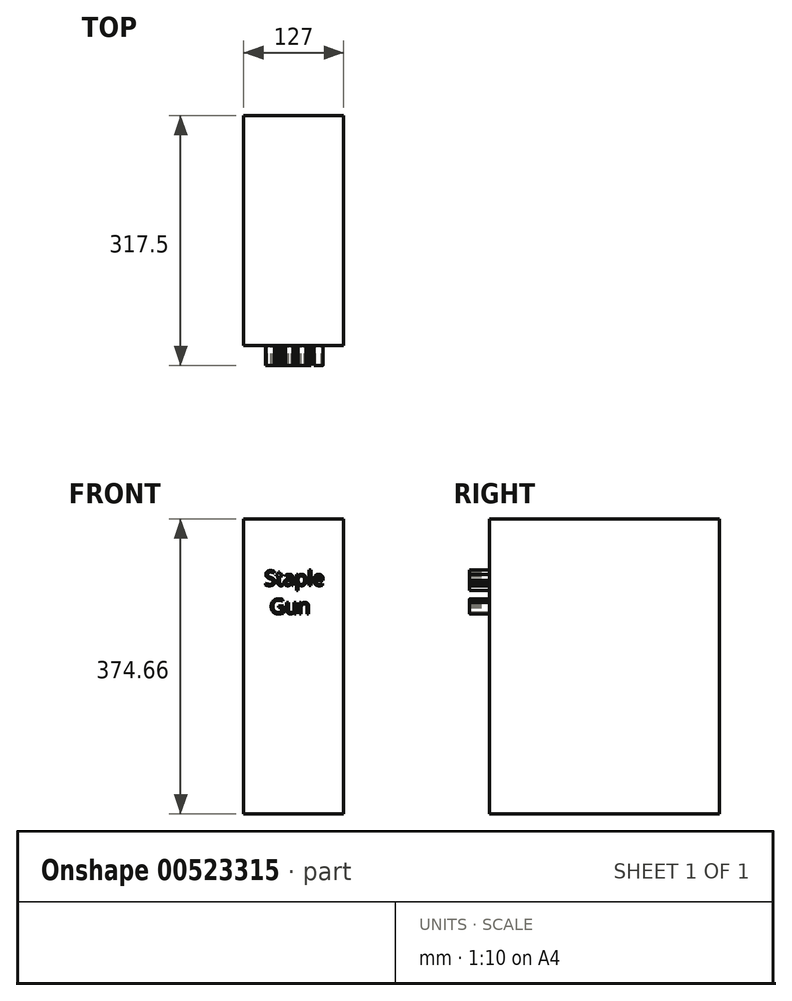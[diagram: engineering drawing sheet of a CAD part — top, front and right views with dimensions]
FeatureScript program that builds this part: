
annotation { "Feature Type Name" : "Feature", "Feature Type Description" : "" }
export const myFeature = defineFeature(function(context is Context, id is Id, definition is map)
    precondition{}
    {
        {
            var Q0;
            Q0=qCreatedBy(makeId("Front.planeOp"),FACE);
            var sketch = newSketch(context, id + "F0", { "sketchPlane" : qUnion([Q0])});
            skLineSegment(sketch, "E0.bottom", {"start": v(63.5, 187.33) * mm, "end": v(-63.5, 187.33) * mm});
            skLineSegment(sketch, "E0.top", {"start": v(63.5, -187.32) * mm, "end": v(-63.5, -187.32) * mm});
            skLineSegment(sketch, "E0.left", {"start": v(63.5, 187.33) * mm, "end": v(63.5, -187.32) * mm});
            skLineSegment(sketch, "E0.right", {"start": v(-63.5, 187.33) * mm, "end": v(-63.5, -187.32) * mm});
            skPoint(sketch, "E0.middle", {"position": v(0, 0) * mm});
            skSolve(sketch);
        }
        {
            var Q0;
            Q0=makeQuery(id+"F0.imprint","IMPRINT",FACE,{"disambiguationData":[TD([[makeQuery(id+"F0.imprint","IMPRINT",EDGE,{"derivedFrom":sQuery(id+"F0.wireOp",EDGE,"E0.bottom")}),1.0]])]});
            extrude(context, id + "F1", {"entities" : qUnion([Q0]), "depth" : 292.1 * mm, "offsetDistance" : 25.4 * mm});
        }
        {
            var Q0;
            Q0=makeQuery(id+"F1.opExtrude","CAP_FACE",FACE,{"disambiguationData":[OSD([sQuery(id+"F0.wireOp",EDGE,"E0.bottom"),sQuery(id+"F0.wireOp",EDGE,"E0.top"),sQuery(id+"F0.wireOp",EDGE,"E0.left"),sQuery(id+"F0.wireOp",EDGE,"E0.right")])],"isStart":false});
            var sketch = newSketch(context, id + "F2", { "sketchPlane" : qUnion([Q0])});
            skText(sketch, "E1", { "text": "Staple\n Gun", "fontName": "OpenSans-Regular.ttf"});
            const initialGuessF2  = {"E1": [-0.03715, 0.10277, 1, 0, 0.01894]};
            skSetInitialGuess(sketch, initialGuessF2);
            skSolve(sketch);
        }
        {
            var Q0;
            Q0 = qSketchRegion(id + "F2", true);
            extrude(context, id + "F3", {"entities" : qUnion([Q0]), "operationType" : NewBodyOperationType.ADD, "depth" : 25.4 * mm, "offsetDistance" : 25.4 * mm});
        }
    });
